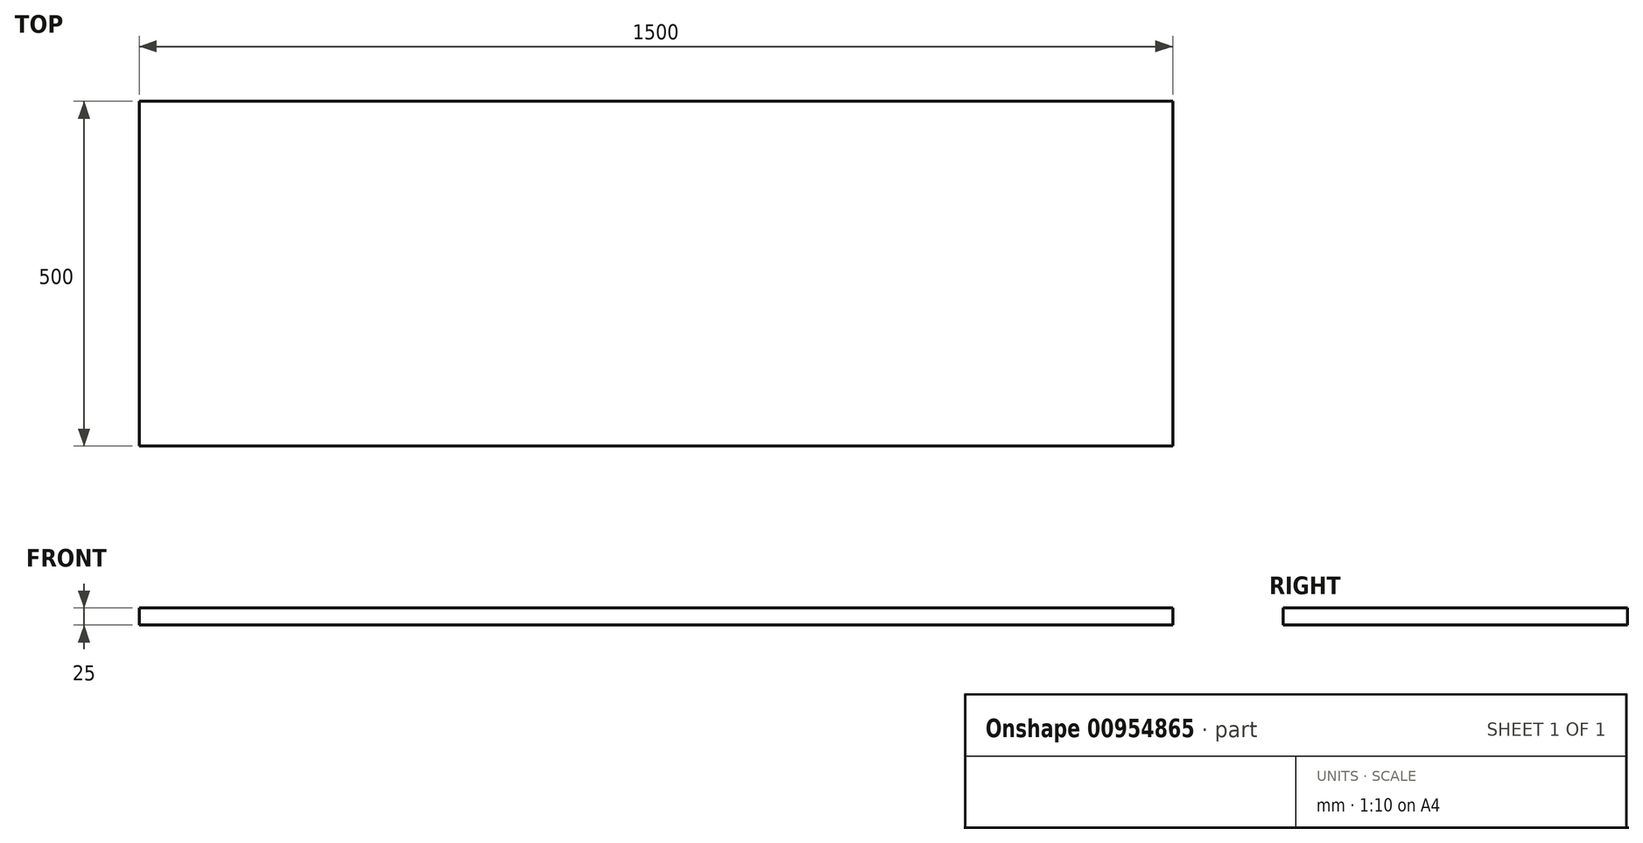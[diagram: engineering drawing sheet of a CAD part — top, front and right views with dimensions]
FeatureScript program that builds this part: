
annotation { "Feature Type Name" : "Feature", "Feature Type Description" : "" }
export const myFeature = defineFeature(function(context is Context, id is Id, definition is map)
    precondition{}
    {
        {
            var Q0;
            Q0=qCreatedBy(makeId("Top.planeOp"),FACE);
            var sketch = newSketch(context, id + "F0", { "sketchPlane" : qUnion([Q0])});
            skLineSegment(sketch, "E0.bottom", {"start": v(-907.65, 179.13) * mm, "end": v(592.35, 179.13) * mm});
            skLineSegment(sketch, "E0.top", {"start": v(-907.65, -320.87) * mm, "end": v(592.35, -320.87) * mm});
            skLineSegment(sketch, "E0.left", {"start": v(-907.65, 179.13) * mm, "end": v(-907.65, -320.87) * mm});
            skLineSegment(sketch, "E0.right", {"start": v(592.35, 179.13) * mm, "end": v(592.35, -320.87) * mm});
            skSolve(sketch);
        }
        {
            var Q0;
            Q0 = qSketchRegion(id + "F0", true);
            extrude(context, id + "F1", {"entities" : qUnion([Q0]), "depth" : 25 * mm, "offsetDistance" : 25 * mm});
        }
        {
            var Q0;
            Q0 = qSketchRegion(id + "F0", true);
            extrude(context, id + "F2", {"entities" : qUnion([Q0]), "operationType" : NewBodyOperationType.ADD, "depth" : 25 * mm, "offsetDistance" : 25 * mm});
        }
        {
            var Q0;
            Q0 = qSketchRegion(id + "F0", true);
            extrude(context, id + "F3", {"entities" : qUnion([Q0]), "operationType" : NewBodyOperationType.ADD, "depth" : 25 * mm, "offsetDistance" : 25 * mm});
        }
    });
